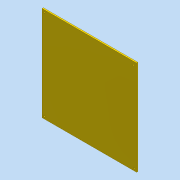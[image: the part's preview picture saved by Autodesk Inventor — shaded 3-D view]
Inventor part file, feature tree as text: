
AUTODESK INVENTOR PART (.ipt)
format: ipt  version: 2016 (Build 200138000, 138)  size: 94,208 bytes
history: native  units: mm
features: hole x4, extrude x1, sketch x1
ambient origin geometry x8: Origin, YZ Plane, XZ Plane, XY Plane, X Axis, Y Axis, Z Axis, Center Point
bodies: Solid1 (feature_tree)
feature tree (6):
  extrude  "Extrusion1"  Depth=220.0mm
  hole  "Hole1"  [1 undecoded]
  hole  "Hole2"  [1 undecoded]
  hole  "Hole3"  [1 undecoded]
  hole  "Hole4"  [1 undecoded]
  sketch  "Sketch1"  dims[d0=220.0mm d1=220.0mm d2=3.0mm d3=0.0mm d4=8.0mm d5=8.0mm d6=3.0mm d7=6.0mm d8=4.0mm d9=2.0mm d10=90.0deg d11=8.0mm d12=20.594885mm d13=5.5mm d14=5.5mm d15=3.0mm d16=6.0mm d17=4.0mm d18=2.0mm d19=90.0deg d20=8.0mm d21=20.594885mm d22=5.5mm d23=5.5mm d24=3.0mm d25=6.0mm d26=4.0mm d27=2.0mm d28=90.0deg d29=8.0mm d30=20.594885mm d31=5.5mm d32=5.5mm d33=3.0mm d34=6.0mm d35=4.0mm d36=2.0mm d37=90.0deg d38=8.0mm d39=20.594885mm]
note: 4 required parameter values undecoded (feature->parameter linkage not recoverable at this tier; creation-order binding heuristic only, values carry confidence <= 0.55)
